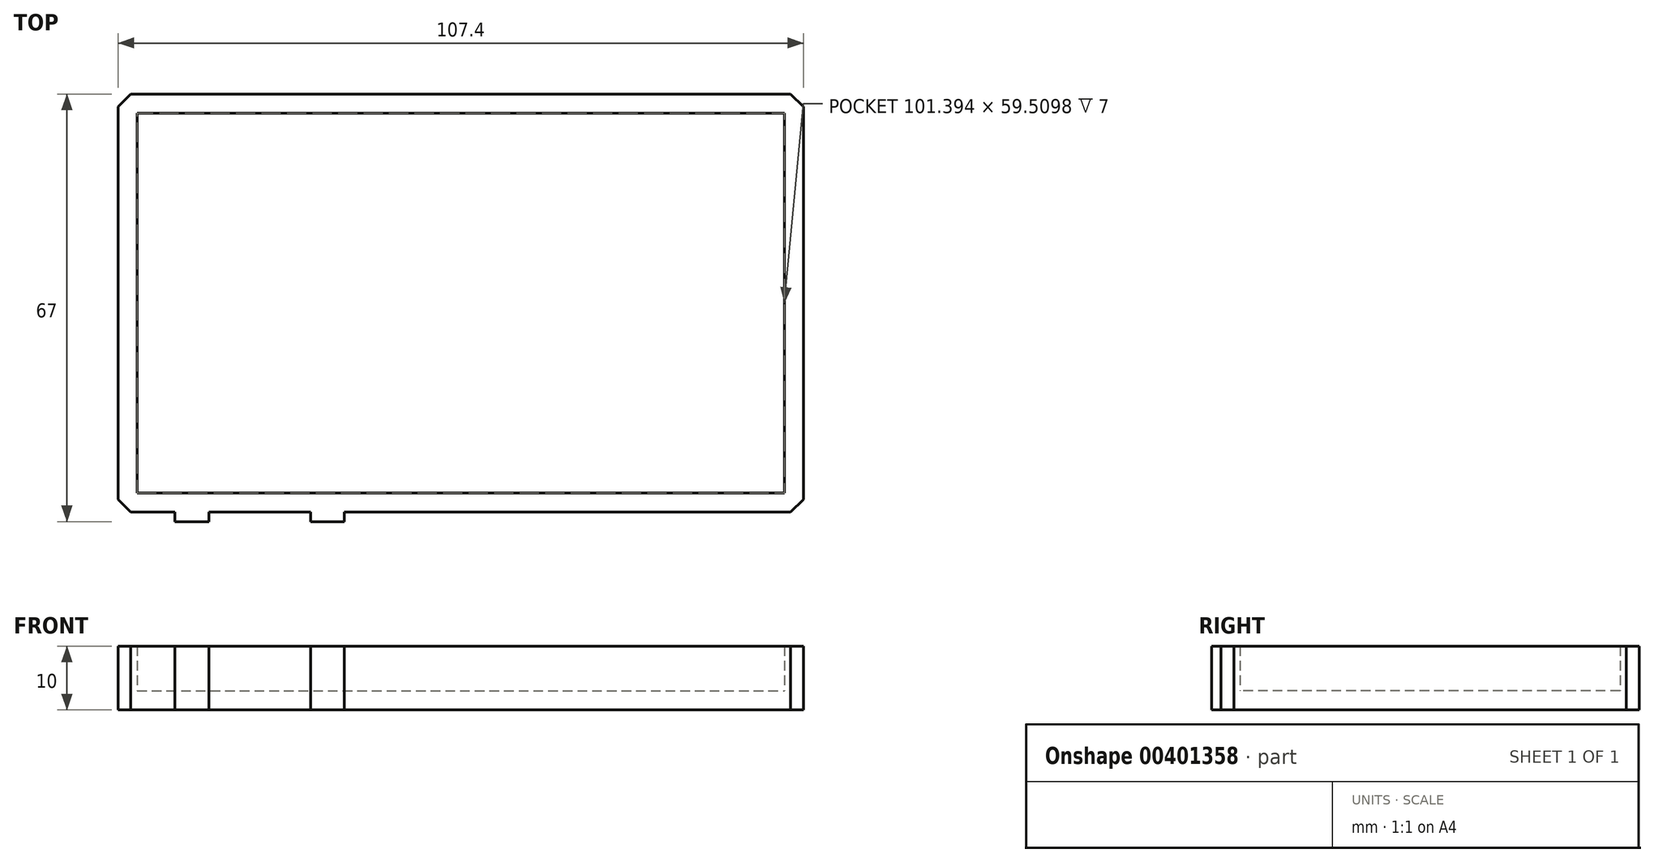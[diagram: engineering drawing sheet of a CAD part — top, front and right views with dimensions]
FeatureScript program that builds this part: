
annotation { "Feature Type Name" : "Feature", "Feature Type Description" : "" }
export const myFeature = defineFeature(function(context is Context, id is Id, definition is map)
    precondition{}
    {
        {
            var Q0;
            Q0=qCreatedBy(makeId("Top.planeOp"),FACE);
            var sketch = newSketch(context, id + "F0", { "sketchPlane" : qUnion([Q0])});
            skLineSegment(sketch, "E0.top", {"start": v(0, 32.75) * mm, "end": v(53.7, 32.75) * mm});
            skLineSegment(sketch, "E0.right", {"start": v(53.7, 0) * mm, "end": v(53.7, 32.75) * mm});
            skLineSegment(sketch, "E1.MirrorCS", {"start": v(0, 32.75) * mm, "end": v(-53.7, 32.75) * mm});
            skLineSegment(sketch, "E2.MirrorCS", {"start": v(-53.7, 0) * mm, "end": v(-53.7, 32.75) * mm});
            skLineSegment(sketch, "E3.MirrorCS", {"start": v(0, -32.75) * mm, "end": v(53.7, -32.75) * mm});
            skLineSegment(sketch, "E4.MirrorCS", {"start": v(53.7, 0) * mm, "end": v(53.7, -32.75) * mm});
            skLineSegment(sketch, "E5.MirrorCS", {"start": v(-53.7, 0) * mm, "end": v(-53.7, -32.75) * mm});
            skLineSegment(sketch, "E6.MirrorCS", {"start": v(0, -32.75) * mm, "end": v(-53.7, -32.75) * mm});
            skSolve(sketch);
        }
        {
            var Q0;
            Q0=makeQuery(id+"F0.imprint","IMPRINT",FACE,{"disambiguationData":[TD([[makeQuery(id+"F0.imprint","IMPRINT",EDGE,{"derivedFrom":sQuery(id+"F0.wireOp",EDGE,"E0.right")}),1.0]])]});
            extrude(context, id + "F1", {"entities" : qUnion([Q0]), "endBound" : BoundingType.SYMMETRIC, "depth" : 10 * mm});
        }
        {
            var Q0;
            Q0=makeQuery(id+"F1.opExtrude","CAP_FACE",FACE,{"disambiguationData":[OSD([sQuery(id+"F0.wireOp",EDGE,"E0.right"),sQuery(id+"F0.wireOp",EDGE,"E1.MirrorCS"),sQuery(id+"F0.wireOp",EDGE,"E2.MirrorCS"),sQuery(id+"F0.wireOp",EDGE,"E0.top"),sQuery(id+"F0.wireOp",EDGE,"E3.MirrorCS"),sQuery(id+"F0.wireOp",EDGE,"E4.MirrorCS"),sQuery(id+"F0.wireOp",EDGE,"E5.MirrorCS"),sQuery(id+"F0.wireOp",EDGE,"E6.MirrorCS")])],"isStart":false});
            shell(context, id + "F2", {"entities" : qUnion([Q0]), "thickness" : 3 * mm});
        }
        {
            var Q0;
            Q0=makeQuery(id+"F1.opExtrude","SWEPT_EDGE",EDGE,{"disambiguationData":[OSD([sQuery(id+"F0.wireOp",EDGE,"E3.MirrorCS"),sQuery(id+"F0.wireOp",EDGE,"E4.MirrorCS")])]});
            var Q1;
            Q1=makeQuery(id+"F1.opExtrude","SWEPT_EDGE",EDGE,{"disambiguationData":[OSD([sQuery(id+"F0.wireOp",EDGE,"E1.MirrorCS"),sQuery(id+"F0.wireOp",EDGE,"E2.MirrorCS")])]});
            var Q2;
            Q2=makeQuery(id+"F1.opExtrude","SWEPT_EDGE",EDGE,{"disambiguationData":[OSD([sQuery(id+"F0.wireOp",EDGE,"E0.right"),sQuery(id+"F0.wireOp",EDGE,"E0.top")])]});
            var Q3;
            Q3=makeQuery(id+"F1.opExtrude","SWEPT_EDGE",EDGE,{"disambiguationData":[OSD([sQuery(id+"F0.wireOp",EDGE,"E5.MirrorCS"),sQuery(id+"F0.wireOp",EDGE,"E6.MirrorCS")])]});
            chamfer(context, id + "F3", {"entities" : qUnion([Q0, Q1, Q2, Q3]), "width" : 2 * mm, "tangentPropagation" : true});
        }
        {
            var Q0;
            Q0=makeQuery(id+"F1.opExtrude","SWEPT_FACE",FACE,{"disambiguationData":[OSD([sQuery(id+"F0.wireOp",EDGE,"E3.MirrorCS"),sQuery(id+"F0.wireOp",EDGE,"E6.MirrorCS")])]});
            var sketch = newSketch(context, id + "F4", { "sketchPlane" : qUnion([Q0])});
            skLineSegment(sketch, "E7.bottom", {"start": v(-39.47, 5) * mm, "end": v(-34.16, 5) * mm});
            skLineSegment(sketch, "E7.top", {"start": v(-39.47, -5) * mm, "end": v(-34.16, -5) * mm});
            skLineSegment(sketch, "E7.left", {"start": v(-39.47, 5) * mm, "end": v(-39.47, -5) * mm});
            skLineSegment(sketch, "E7.right", {"start": v(-34.16, 5) * mm, "end": v(-34.16, -5) * mm});
            skLineSegment(sketch, "E8.MirrorCS", {"start": v(-44.78, 5) * mm, "end": v(-44.78, -5) * mm});
            skLineSegment(sketch, "E9.MirrorCS", {"start": v(-34.16, 40) * mm, "end": v(-34.16, -40) * mm});
            skLineSegment(sketch, "E10.MirrorCS", {"start": v(-28.85, 5) * mm, "end": v(-28.85, -5) * mm});
            skLineSegment(sketch, "E11.MirrorCS", {"start": v(-28.85, 40) * mm, "end": v(-28.85, -40) * mm});
            skLineSegment(sketch, "E12.MirrorCS", {"start": v(-23.54, 40) * mm, "end": v(-23.54, -40) * mm});
            skLineSegment(sketch, "E13.MirrorCS", {"start": v(-18.23, 40) * mm, "end": v(-18.23, -40) * mm});
            skSolve(sketch);
        }
        {
            var Q0;
            {var subQ0=sQuery(id+"F4.wireOp",EDGE,"E8.MirrorCS");Q0=makeQuery(id+"F4.imprint","IMPRINT",FACE,{"disambiguationData":[TD([[makeQuery(id+"F4.imprint","IMPRINT",EDGE,{"derivedFrom":subQ0}),1.0]])]});}
            var Q1;
            {var subQ0=sQuery(id+"F4.wireOp",EDGE,"E11.MirrorCS");Q1=makeQuery(id+"F4.imprint","IMPRINT",FACE,{"disambiguationData":[TD([[makeQuery(id+"F4.imprint","IMPRINT",EDGE,{"derivedFrom":subQ0}),-1.0]])]});}
            var Q2;
            {var subQ0=sQuery(id+"F4.wireOp",EDGE,"E13.MirrorCS");Q2=makeQuery(id+"F4.imprint","IMPRINT",FACE,{"disambiguationData":[TD([[makeQuery(id+"F4.imprint","IMPRINT",EDGE,{"derivedFrom":subQ0}),-1.0]])]});}
            var Q3;
            Q3=sQuery(id+"F4.wireOp",EDGE,"E13.MirrorCS");
            var Q4;
            Q4=sQuery(id+"F4.wireOp",EDGE,"E8.MirrorCS");
            var Q5;
            Q5=sQuery(id+"F4.wireOp",EDGE,"E12.MirrorCS");
            var Q6;
            Q6=sQuery(id+"F4.wireOp",EDGE,"E7.left");
            var Q7;
            Q7=sQuery(id+"F4.wireOp",EDGE,"E9.MirrorCS");
            var Q8;
            Q8=sQuery(id+"F4.wireOp",EDGE,"E11.MirrorCS");
            extrude(context, id + "F5", {"entities" : qUnion([Q0, Q1, Q2]), "operationType" : NewBodyOperationType.ADD, "surfaceEntities" : qUnion([Q3, Q4, Q5, Q6, Q7, Q8]), "depth" : 1.5 * mm});
        }
    });
